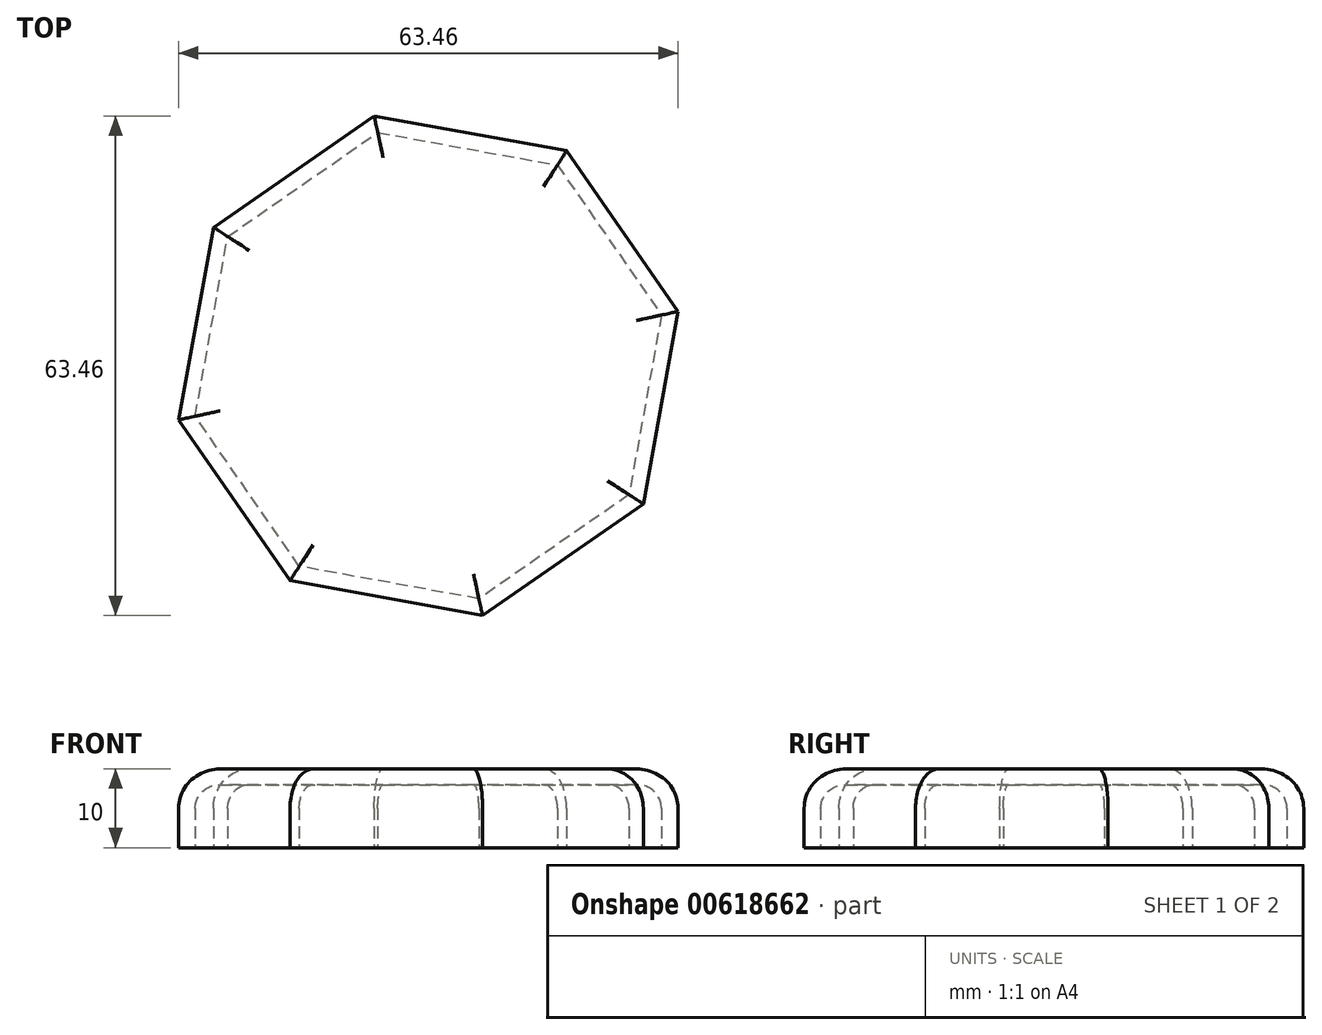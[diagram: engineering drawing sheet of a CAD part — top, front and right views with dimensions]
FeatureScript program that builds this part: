
annotation { "Feature Type Name" : "Feature", "Feature Type Description" : "" }
export const myFeature = defineFeature(function(context is Context, id is Id, definition is map)
    precondition{}
    {
        {
            var Q0;
            Q0=qCreatedBy(makeId("Top.planeOp"),FACE);
            var sketch = newSketch(context, id + "F0", { "sketchPlane" : qUnion([Q0])});
            skCircle(sketch, "E0.cCircle", {"center": v(0, 5.29) * mm, "radius": 30 * mm, "construction": true});
            skLineSegment(sketch, "E0.0", {"start": v(-31.73, -1.6) * mm, "end": v(-27.3, 22.86) * mm});
            skLineSegment(sketch, "E0.1", {"start": v(-27.3, 22.86) * mm, "end": v(-6.89, 37.02) * mm});
            skLineSegment(sketch, "E0.2", {"start": v(-6.89, 37.02) * mm, "end": v(17.57, 32.6) * mm});
            skLineSegment(sketch, "E0.3", {"start": v(17.57, 32.6) * mm, "end": v(31.73, 12.18) * mm});
            skLineSegment(sketch, "E0.4", {"start": v(31.73, 12.18) * mm, "end": v(27.3, -12.28) * mm});
            skLineSegment(sketch, "E0.5", {"start": v(27.3, -12.28) * mm, "end": v(6.89, -26.44) * mm});
            skLineSegment(sketch, "E0.6", {"start": v(6.89, -26.44) * mm, "end": v(-17.57, -22.02) * mm});
            skLineSegment(sketch, "E0.7", {"start": v(-17.57, -22.02) * mm, "end": v(-31.73, -1.6) * mm});
            skPoint(sketch, "E0.0.midPoint", {"position": v(-29.52, 10.63) * mm});
            skSolve(sketch);
        }
        {
            var Q0;
            Q0 = qSketchRegion(id + "F0", true);
            extrude(context, id + "F1", {"entities" : qUnion([Q0]), "depth" : 10 * mm, "offsetDistance" : 25 * mm});
        }
        {
            var Q0;
            Q0=makeQuery(id+"F1.opExtrude","CAP_EDGE",EDGE,{"disambiguationData":[OSD([sQuery(id+"F0.wireOp",EDGE,"E0.6")])],"isStart":false});
            var Q1;
            Q1=makeQuery(id+"F1.opExtrude","CAP_EDGE",EDGE,{"disambiguationData":[OSD([sQuery(id+"F0.wireOp",EDGE,"E0.5")])],"isStart":false});
            var Q2;
            Q2=makeQuery(id+"F1.opExtrude","CAP_EDGE",EDGE,{"disambiguationData":[OSD([sQuery(id+"F0.wireOp",EDGE,"E0.4")])],"isStart":false});
            var Q3;
            Q3=makeQuery(id+"F1.opExtrude","CAP_EDGE",EDGE,{"disambiguationData":[OSD([sQuery(id+"F0.wireOp",EDGE,"E0.3")])],"isStart":false});
            var Q4;
            Q4=makeQuery(id+"F1.opExtrude","CAP_EDGE",EDGE,{"disambiguationData":[OSD([sQuery(id+"F0.wireOp",EDGE,"E0.2")])],"isStart":false});
            var Q5;
            Q5=makeQuery(id+"F1.opExtrude","CAP_EDGE",EDGE,{"disambiguationData":[OSD([sQuery(id+"F0.wireOp",EDGE,"E0.1")])],"isStart":false});
            var Q6;
            Q6=makeQuery(id+"F1.opExtrude","CAP_EDGE",EDGE,{"disambiguationData":[OSD([sQuery(id+"F0.wireOp",EDGE,"E0.0")])],"isStart":false});
            var Q7;
            Q7=makeQuery(id+"F1.opExtrude","CAP_EDGE",EDGE,{"disambiguationData":[OSD([sQuery(id+"F0.wireOp",EDGE,"E0.7")])],"isStart":false});
            fillet(context, id + "F2", {"entities" : qUnion([Q0, Q1, Q2, Q3, Q4, Q5, Q6, Q7]), "radius" : 5 * mm, "tangentPropagation" : true, "allowEdgeOverflow" : false});
        }
        {
            var Q0;
            Q0=makeQuery(id+"F1.opExtrude","CAP_FACE",FACE,{"disambiguationData":[OSD([sQuery(id+"F0.wireOp",EDGE,"E0.0"),sQuery(id+"F0.wireOp",EDGE,"E0.1"),sQuery(id+"F0.wireOp",EDGE,"E0.2"),sQuery(id+"F0.wireOp",EDGE,"E0.3"),sQuery(id+"F0.wireOp",EDGE,"E0.4"),sQuery(id+"F0.wireOp",EDGE,"E0.5"),sQuery(id+"F0.wireOp",EDGE,"E0.6"),sQuery(id+"F0.wireOp",EDGE,"E0.7")])],"isStart":true});
            shell(context, id + "F3", {"entities" : qUnion([Q0]), "thickness" : 2 * mm});
        }
    });
